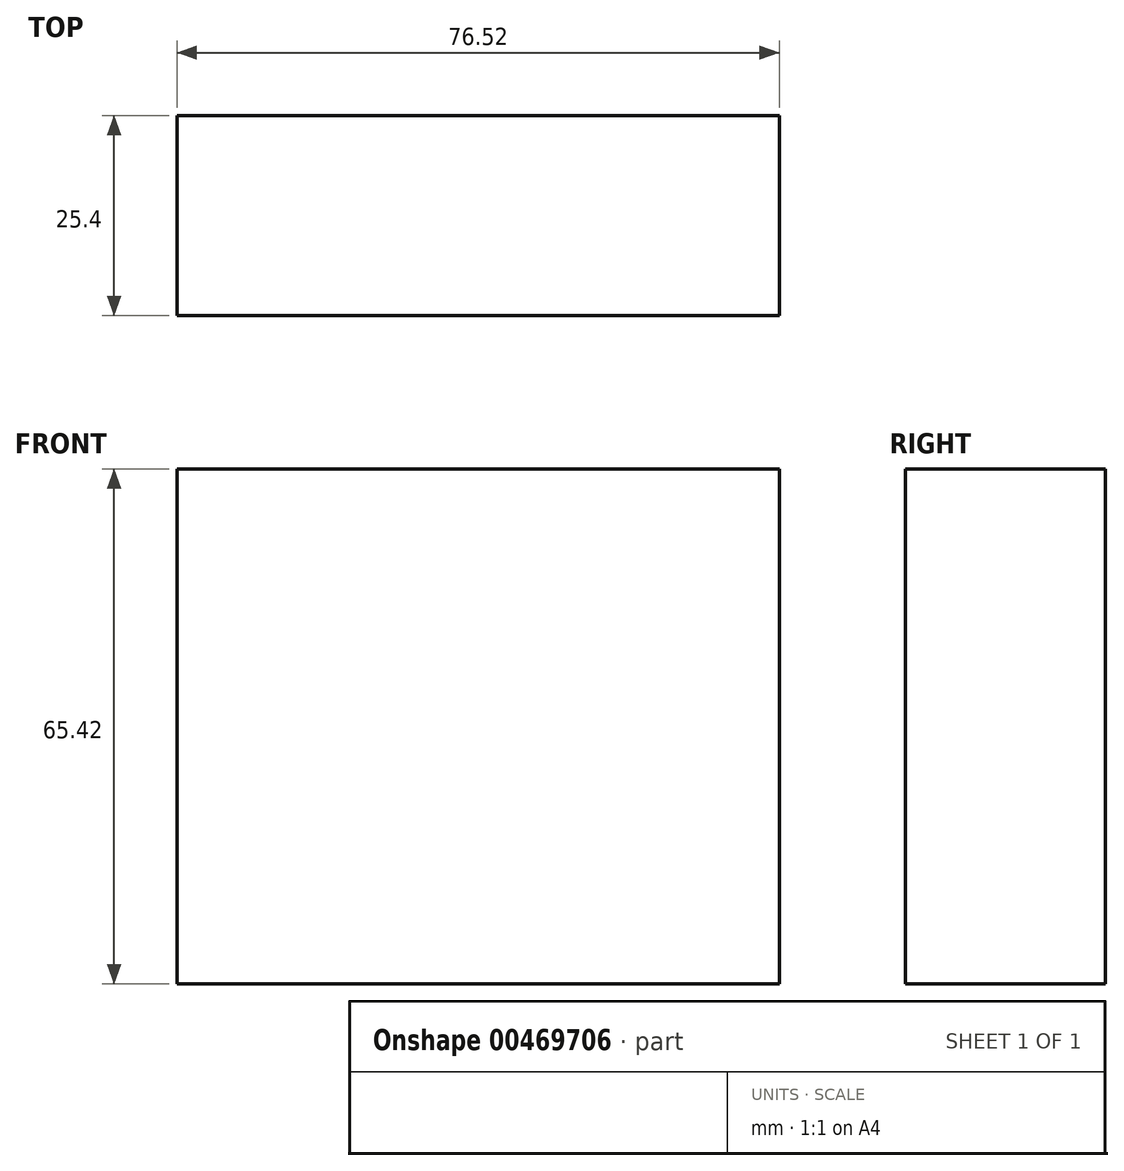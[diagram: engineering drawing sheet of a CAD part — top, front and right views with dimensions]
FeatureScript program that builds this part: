
annotation { "Feature Type Name" : "Feature", "Feature Type Description" : "" }
export const myFeature = defineFeature(function(context is Context, id is Id, definition is map)
    precondition{}
    {
        {
            var Q0;
            Q0=qCreatedBy(makeId("Front.planeOp"),FACE);
            var sketch = newSketch(context, id + "F0", { "sketchPlane" : qUnion([Q0])});
            skLineSegment(sketch, "E0.bottom", {"start": v(-44.07, 41.04) * mm, "end": v(32.45, 41.04) * mm});
            skLineSegment(sketch, "E0.top", {"start": v(-44.07, -24.38) * mm, "end": v(32.45, -24.38) * mm});
            skLineSegment(sketch, "E0.left", {"start": v(-44.07, 41.04) * mm, "end": v(-44.07, -24.38) * mm});
            skLineSegment(sketch, "E0.right", {"start": v(32.45, 41.04) * mm, "end": v(32.45, -24.38) * mm});
            skSolve(sketch);
        }
        {
            var Q0;
            Q0 = qSketchRegion(id + "F0", true);
            extrude(context, id + "F1", {"entities" : qUnion([Q0]), "depth" : 25.4 * mm});
        }
    });
